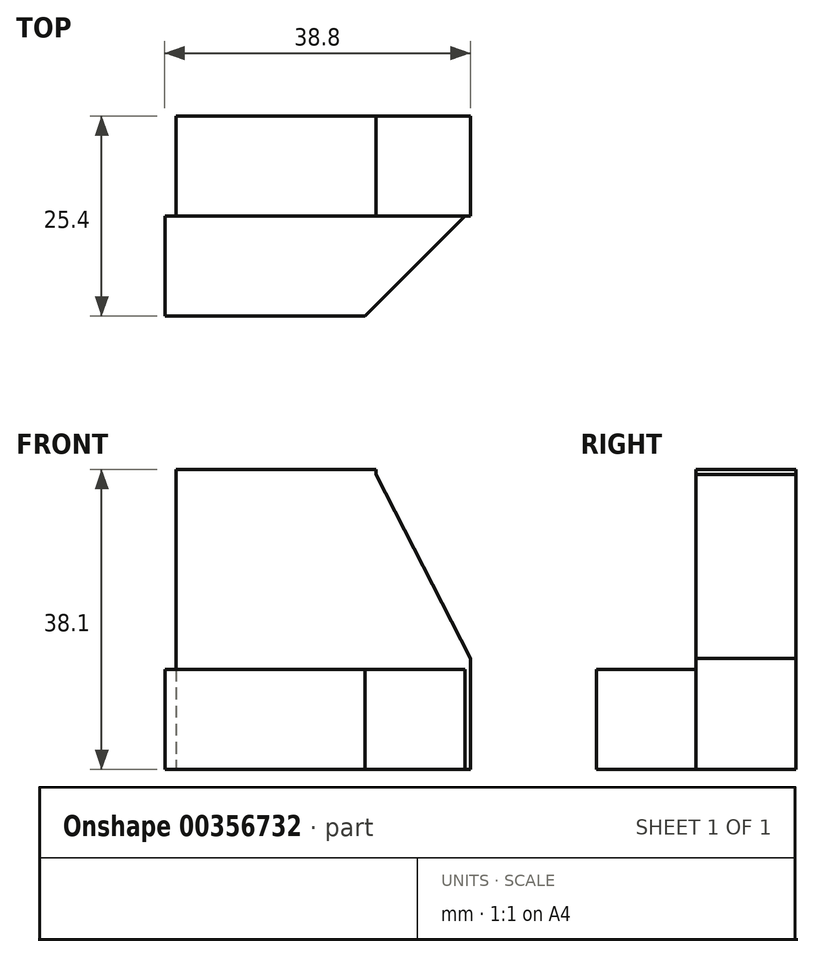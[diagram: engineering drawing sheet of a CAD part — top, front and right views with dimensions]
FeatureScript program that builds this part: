
annotation { "Feature Type Name" : "Feature", "Feature Type Description" : "" }
export const myFeature = defineFeature(function(context is Context, id is Id, definition is map)
    precondition{}
    {
        {
            var Q0;
            Q0=qCreatedBy(makeId("Top.planeOp"),FACE);
            var sketch = newSketch(context, id + "F0", { "sketchPlane" : qUnion([Q0])});
            skLineSegment(sketch, "E0", {"start": v(-47.78, 0) * mm, "end": v(-47.78, -12.7) * mm});
            skLineSegment(sketch, "E1", {"start": v(-47.78, -12.7) * mm, "end": v(-22.38, -12.7) * mm});
            skLineSegment(sketch, "E2", {"start": v(-47.78, 0) * mm, "end": v(-9.68, 0) * mm});
            skLineSegment(sketch, "E3", {"start": v(-9.68, 0) * mm, "end": v(-22.38, -12.7) * mm});
            skSolve(sketch);
        }
        {
            var Q0;
            Q0=makeQuery(id+"F0.imprint","IMPRINT",FACE,{"disambiguationData":[TD([[makeQuery(id+"F0.imprint","IMPRINT",EDGE,{"derivedFrom":sQuery(id+"F0.wireOp",EDGE,"E0")}),1.0]])]});
            extrude(context, id + "F1", {"entities" : qUnion([Q0]), "depth" : 12.7 * mm});
        }
        {
            var Q0;
            Q0=qCreatedBy(makeId("Top.planeOp"),FACE);
            var sketch = newSketch(context, id + "F2", { "sketchPlane" : qUnion([Q0])});
            skLineSegment(sketch, "E4", {"start": v(-46.37, 12.7) * mm, "end": v(-20.97, 12.7) * mm});
            skLineSegment(sketch, "E5", {"start": v(-20.97, 12.7) * mm, "end": v(-20.97, 0) * mm});
            skLineSegment(sketch, "E6", {"start": v(-46.37, 0) * mm, "end": v(-20.97, 0) * mm});
            skLineSegment(sketch, "E7", {"start": v(-46.37, 12.7) * mm, "end": v(-46.37, 0) * mm});
            skSolve(sketch);
        }
        {
            var Q0;
            Q0=makeQuery(id+"F2.imprint","IMPRINT",FACE,{"disambiguationData":[TD([[makeQuery(id+"F2.imprint","IMPRINT",EDGE,{"derivedFrom":sQuery(id+"F2.wireOp",EDGE,"oVfEGzoz-soWz-wiSE-yX6w-jea6bPWlpqQq")}),-1.0]])]});
            var Q1;
            Q1=makeQuery(id+"F2.imprint","IMPRINT",FACE,{"disambiguationData":[TD([[makeQuery(id+"F2.imprint","IMPRINT",EDGE,{"derivedFrom":sQuery(id+"F2.wireOp",EDGE,"E4")}),-1.0]])]});
            extrude(context, id + "F3", {"entities" : qUnion([Q0, Q1]), "operationType" : NewBodyOperationType.ADD, "depth" : 38.1 * mm});
        }
        {
            var Q0;
            Q0=qCreatedBy(makeId("Front.planeOp"),FACE);
            var sketch = newSketch(context, id + "F4", { "sketchPlane" : qUnion([Q0])});
            skLineSegment(sketch, "E8", {"start": v(-21.36, 0) * mm, "end": v(-8.98, 0) * mm});
            skLineSegment(sketch, "E9", {"start": v(-8.98, 0) * mm, "end": v(-8.98, 14.08) * mm});
            skLineSegment(sketch, "E10", {"start": v(-8.98, 14.08) * mm, "end": v(-21.05, 37.6) * mm});
            skLineSegment(sketch, "E11", {"start": v(-21.05, 37.6) * mm, "end": v(-21.36, 0) * mm});
            skSolve(sketch);
        }
        {
            var Q0;
            Q0=makeQuery(id+"F4.imprint","IMPRINT",FACE,{"disambiguationData":[TD([[makeQuery(id+"F4.imprint","IMPRINT",EDGE,{"derivedFrom":sQuery(id+"F4.wireOp",EDGE,"E8")}),1.0]])]});
            extrude(context, id + "F5", {"entities" : qUnion([Q0]), "operationType" : NewBodyOperationType.ADD, "oppositeDirection" : true, "depth" : 12.7 * mm});
        }
    });
